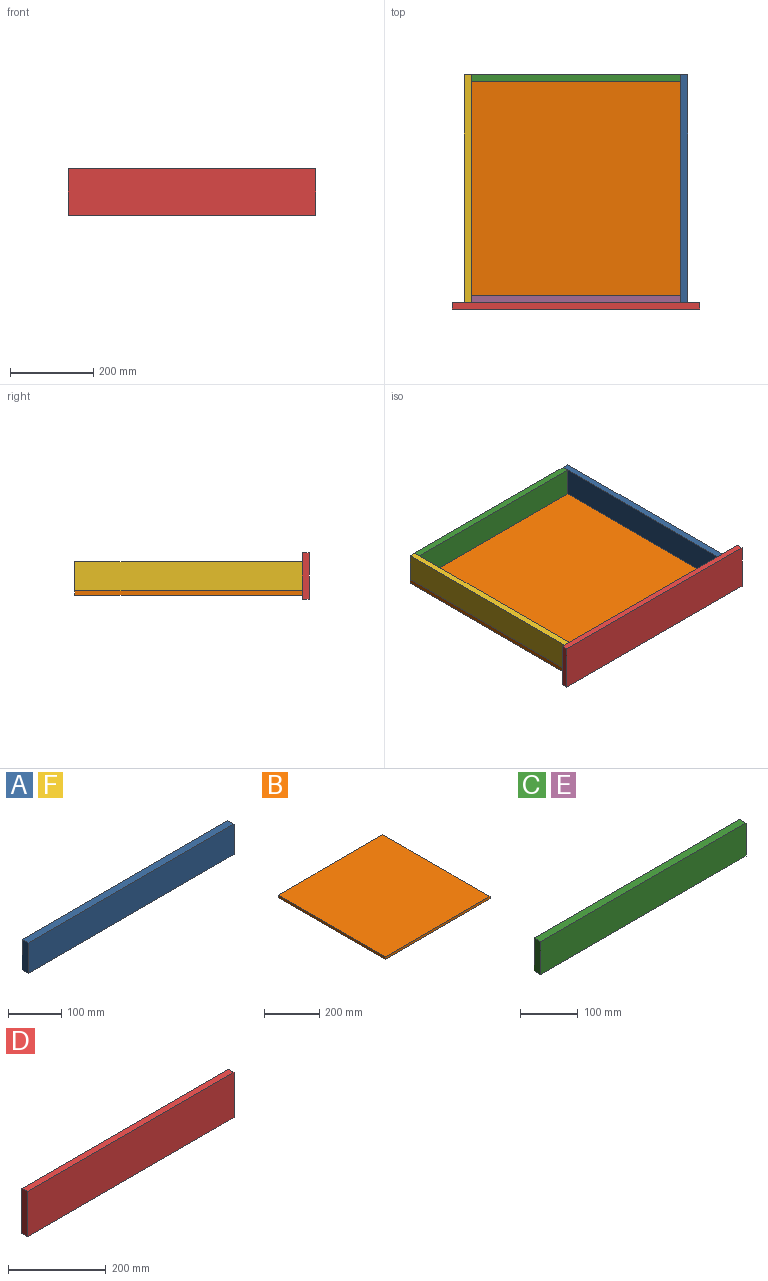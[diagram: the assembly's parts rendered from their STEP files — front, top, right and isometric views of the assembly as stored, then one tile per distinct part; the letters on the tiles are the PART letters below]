
ASSEMBLY  parts=6 mates=5
PART A: 6 faces, bbox 548x16x70 mm
  f0: plane 548x16mm, normal (0,0,1), area 8768mm2, adj f1,f3,f4,f5
  f1: plane 70x16mm, normal (-1,0,0), area 1120mm2, adj f0,f2,f4,f5
  f2: plane 548x16mm, normal (0,0,-1), area 8768mm2, adj f1,f3,f4,f5
  f3: plane 70x16mm, normal (1,0,0), area 1120mm2, adj f0,f2,f4,f5
  f4: plane 548x70mm, normal (0,-1,0), area 38360mm2, adj f0,f1,f2,f3
  f5: plane 548x70mm, normal (0,1,0), area 38360mm2, adj f0,f1,f2,f3
PART B: 6 faces, bbox 537x548x11 mm
  f0: plane 537x11mm, normal (0,1,0), area 5907mm2, adj f1,f3,f4,f5
  f1: plane 548x11mm, normal (-1,0,0), area 6028mm2, adj f0,f2,f4,f5
  f2: plane 537x11mm, normal (0,-1,0), area 5907mm2, adj f1,f3,f4,f5
  f3: plane 548x11mm, normal (1,0,0), area 6028mm2, adj f0,f2,f4,f5
  f4: plane 548x537mm, normal (0,0,-1), area 294276mm2, adj f0,f1,f2,f3
  f5: plane 548x537mm, normal (0,0,1), area 294276mm2, adj f0,f1,f2,f3
PART C: 6 faces, bbox 505x16x70 mm
  f0: plane 505x16mm, normal (0,0,1), area 8080mm2, adj f1,f3,f4,f5
  f1: plane 70x16mm, normal (-1,0,0), area 1120mm2, adj f0,f2,f4,f5
  f2: plane 505x16mm, normal (0,0,-1), area 8080mm2, adj f1,f3,f4,f5
  f3: plane 70x16mm, normal (1,0,0), area 1120mm2, adj f0,f2,f4,f5
  f4: plane 505x70mm, normal (0,-1,0), area 35350mm2, adj f0,f1,f2,f3
  f5: plane 505x70mm, normal (0,1,0), area 35350mm2, adj f0,f1,f2,f3
PART D: 6 faces, bbox 596x16x113 mm
  f0: plane 596x16mm, normal (0,0,1), area 9536mm2, adj f1,f3,f4,f5
  f1: plane 113x16mm, normal (-1,0,0), area 1808mm2, adj f0,f2,f4,f5
  f2: plane 596x16mm, normal (0,0,-1), area 9536mm2, adj f1,f3,f4,f5
  f3: plane 113x16mm, normal (1,0,0), area 1808mm2, adj f0,f2,f4,f5
  f4: plane 596x113mm, normal (0,-1,0), area 67348mm2, adj f0,f1,f2,f3
  f5: plane 596x113mm, normal (0,1,0), area 67348mm2, adj f0,f1,f2,f3
PART E: same geometry as C
PART F: same geometry as A
PLACE A rot(axis=(0.71,-0.71,0),180deg) t=(216.9,249.7,32.12)mm
PLACE B t=(-35.6,249.7,-2.88)mm
PLACE C t=(-35.6,523.7,32.12)mm
PLACE D t=(-35.6,-24.3,32.62)mm fixed
PLACE E t=(-35.6,-8.3,32.12)mm
PLACE F rot(axis=(0.71,0.71,0),180deg) t=(-288.1,249.7,32.12)mm
MATE fastened A.f0 <-> B.f5  axis (0,0,-1) through (232.9,249.7,-2.88)mm
MATE fastened E.f2 <-> B.f5  axis (0,0,-1) through (-35.6,-24.3,-2.88)mm
MATE fastened B.f2 <-> D.f5  axis (0,-1,0) through (-35.6,-24.3,-13.88)mm
MATE fastened C.f2 <-> B.f5  axis (0,0,-1) through (-35.6,523.7,-2.88)mm
MATE fastened F.f0 <-> B.f5  axis (0,0,-1) through (-304.1,249.7,-2.88)mm
